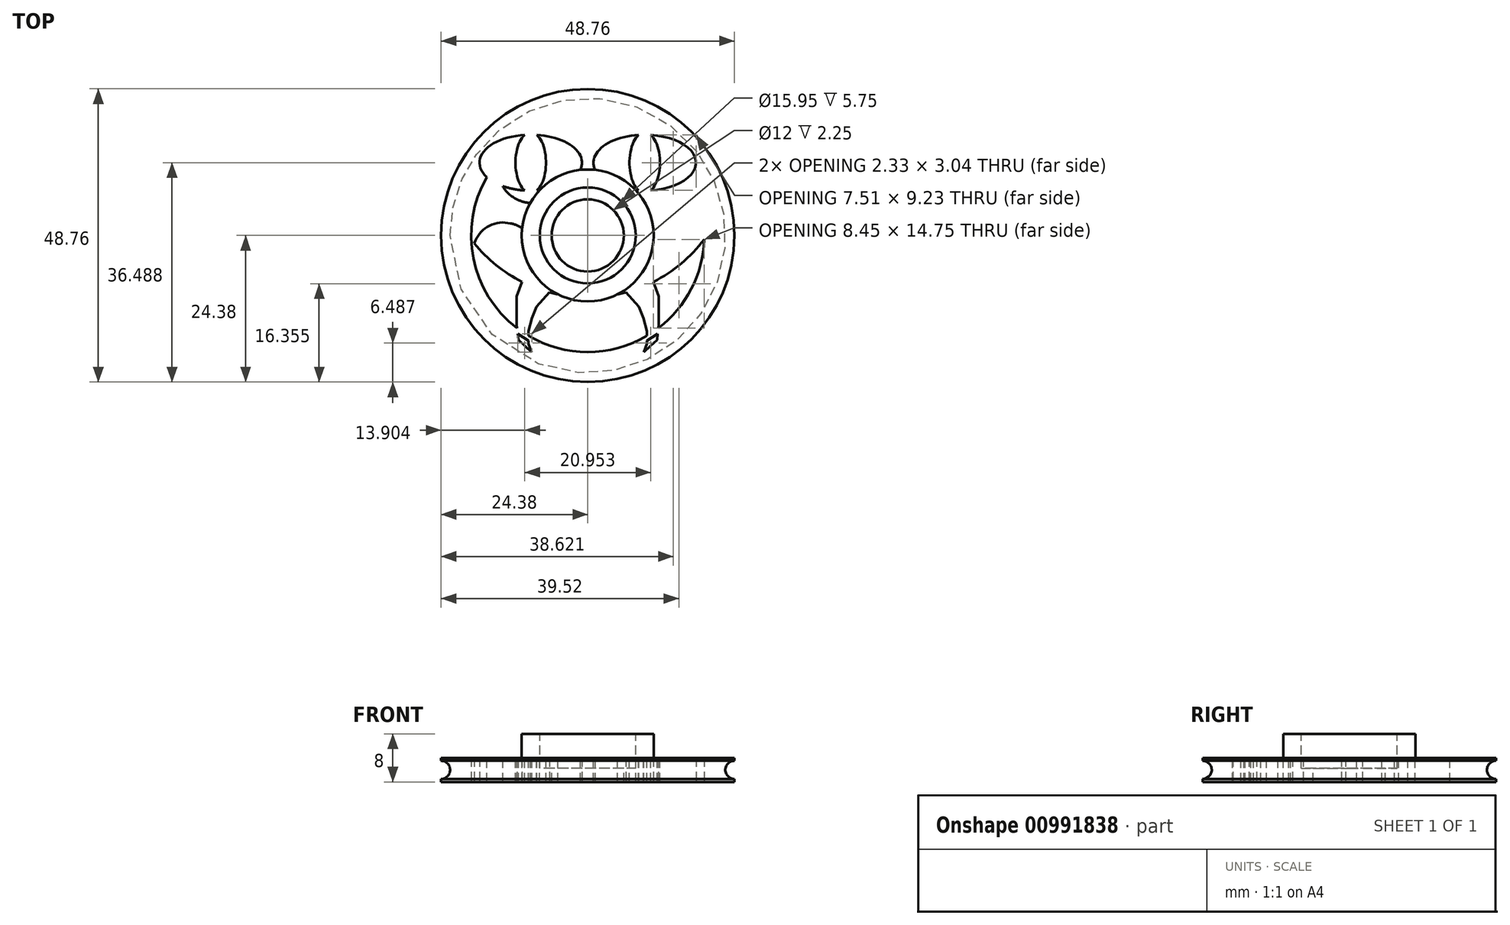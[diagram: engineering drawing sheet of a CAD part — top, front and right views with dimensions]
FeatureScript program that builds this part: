
annotation { "Feature Type Name" : "Feature", "Feature Type Description" : "" }
export const myFeature = defineFeature(function(context is Context, id is Id, definition is map)
    precondition{}
    {
        {
            var Q0;
            Q0=qCreatedBy(makeId("Top.planeOp"),FACE);
            var sketch = newSketch(context, id + "F0", { "sketchPlane" : qUnion([Q0])});
            skCircle(sketch, "E0", {"center": v(0, 0) * mm, "radius": 24.38 * mm});
            skCircle(sketch, "E1", {"center": v(0, 0) * mm, "radius": 8 * mm});
            skArc(sketch, "E2", {"start": v(-4.5, 7.8) * mm, "mid": v(0, -9) * mm, "end": v(4.5, 7.8) * mm});
            skArc(sketch, "E3.0", {"start": v(-9.52, 16.88) * mm, "mid": v(0, -19.38) * mm, "end": v(9.52, 16.88) * mm});
            skLineSegment(sketch, "E4.0", {"start": v(-2.12, 13.29) * mm, "end": v(-2.06, 12.89) * mm});
            skLineSegment(sketch, "E5.0", {"start": v(2.12, 13.29) * mm, "end": v(2.06, 12.89) * mm});
            skPoint(sketch, "E6.orphan", {"position": v(0, 21.65) * mm});
            skPoint(sketch, "E7.visualSharp", {"position": v(-1.44, 8.88) * mm});
            skArc(sketch, "E7.filletArc", {"start": v(-4.5, 7.8) * mm, "mid": v(-2.5, 9.96) * mm, "end": v(-2.06, 12.89) * mm});
            skPoint(sketch, "E8.visualSharp", {"position": v(1.44, 8.88) * mm});
            skArc(sketch, "E8.filletArc", {"start": v(2.06, 12.89) * mm, "mid": v(2.5, 9.96) * mm, "end": v(4.5, 7.8) * mm});
            skPoint(sketch, "E9.visualSharp", {"position": v(3.03, 19.14) * mm});
            skArc(sketch, "E9.filletArc", {"start": v(9.52, 16.88) * mm, "mid": v(4.88, 17.02) * mm, "end": v(2.12, 13.29) * mm});
            skPoint(sketch, "E10.visualSharp", {"position": v(-3.03, 19.14) * mm});
            skArc(sketch, "E10.filletArc", {"start": v(-2.12, 13.29) * mm, "mid": v(-4.88, 17.02) * mm, "end": v(-9.52, 16.88) * mm});
            skArc(sketch, "E11.1.0", {"start": v(-13.3, 2.09) * mm, "mid": v(-17.7, 0.62) * mm, "end": v(-19, -3.84) * mm});
            skLineSegment(sketch, "E11.1.1", {"start": v(-13.3, 2.09) * mm, "end": v(-12.9, 2.02) * mm});
            skArc(sketch, "E11.1.2", {"start": v(-8.8, -1.87) * mm, "mid": v(-10.25, 0.71) * mm, "end": v(-12.9, 2.02) * mm});
            skArc(sketch, "E11.1.3", {"start": v(-11.62, 5.94) * mm, "mid": v(-8.7, 5.45) * mm, "end": v(-6.02, 6.69) * mm});
            skLineSegment(sketch, "E11.1.4", {"start": v(-11.98, 6.12) * mm, "end": v(-11.62, 5.94) * mm});
            skArc(sketch, "E11.1.5", {"start": v(-13.1, 14.27) * mm, "mid": v(-14.68, 9.9) * mm, "end": v(-11.98, 6.12) * mm});
            skArc(sketch, "E11.2.0", {"start": v(-6.1, -12) * mm, "mid": v(-6.06, -16.64) * mm, "end": v(-2.22, -19.25) * mm});
            skLineSegment(sketch, "E11.2.1", {"start": v(-6.1, -12) * mm, "end": v(-5.91, -11.64) * mm});
            skArc(sketch, "E11.2.2", {"start": v(-0.94, -8.95) * mm, "mid": v(-3.84, -9.53) * mm, "end": v(-5.91, -11.64) * mm});
            skArc(sketch, "E11.2.3", {"start": v(-9.24, -9.22) * mm, "mid": v(-7.87, -6.6) * mm, "end": v(-8.22, -3.66) * mm});
            skLineSegment(sketch, "E11.2.4", {"start": v(-9.52, -9.5) * mm, "end": v(-9.24, -9.22) * mm});
            skArc(sketch, "E11.2.5", {"start": v(-17.62, -8.06) * mm, "mid": v(-13.95, -10.9) * mm, "end": v(-9.52, -9.5) * mm});
            skArc(sketch, "E11.3.0", {"start": v(9.52, -9.5) * mm, "mid": v(13.95, -10.9) * mm, "end": v(17.62, -8.06) * mm});
            skLineSegment(sketch, "E11.3.1", {"start": v(9.52, -9.5) * mm, "end": v(9.24, -9.22) * mm});
            skArc(sketch, "E11.3.2", {"start": v(8.22, -3.66) * mm, "mid": v(7.87, -6.6) * mm, "end": v(9.24, -9.22) * mm});
            skArc(sketch, "E11.3.3", {"start": v(5.91, -11.64) * mm, "mid": v(3.84, -9.53) * mm, "end": v(0.94, -8.95) * mm});
            skLineSegment(sketch, "E11.3.4", {"start": v(6.1, -12) * mm, "end": v(5.91, -11.64) * mm});
            skArc(sketch, "E11.3.5", {"start": v(2.22, -19.25) * mm, "mid": v(6.06, -16.64) * mm, "end": v(6.1, -12) * mm});
            skArc(sketch, "E11.4.0", {"start": v(11.98, 6.12) * mm, "mid": v(14.68, 9.9) * mm, "end": v(13.1, 14.27) * mm});
            skLineSegment(sketch, "E11.4.1", {"start": v(11.98, 6.12) * mm, "end": v(11.62, 5.94) * mm});
            skArc(sketch, "E11.4.2", {"start": v(6.02, 6.69) * mm, "mid": v(8.7, 5.45) * mm, "end": v(11.62, 5.94) * mm});
            skArc(sketch, "E11.4.3", {"start": v(12.9, 2.02) * mm, "mid": v(10.25, 0.71) * mm, "end": v(8.8, -1.87) * mm});
            skLineSegment(sketch, "E11.4.4", {"start": v(13.3, 2.09) * mm, "end": v(12.9, 2.02) * mm});
            skArc(sketch, "E11.4.5", {"start": v(19, -3.84) * mm, "mid": v(17.7, 0.62) * mm, "end": v(13.3, 2.09) * mm});
            skCircle(sketch, "E12", {"center": v(0, 13.95) * mm, "radius": 24.25 * mm});
            skSolve(sketch);
        }
        {
            var Q0;
            Q0=makeQuery(id+"F0.imprint","IMPRINT",FACE,{"disambiguationData":[TD([[makeQuery(id+"F0.imprint","IMPRINT",EDGE,{"derivedFrom":sQuery(id+"F0.wireOp",EDGE,"E0")}),1.0]])]});
            var Q1;
            {var subQ0=sQuery(id+"F0.wireOp",EDGE,"E11.4.0");Q1=makeQuery(id+"F0.imprint","IMPRINT",FACE,{"disambiguationData":[TD([[makeQuery(id+"F0.imprint","IMPRINT",EDGE,{"derivedFrom":subQ0}),-1.0]])]});}
            var Q2;
            Q2=makeQuery(id+"F0.imprint","IMPRINT",FACE,{"disambiguationData":[TD([[makeQuery(id+"F0.imprint","IMPRINT",EDGE,{"derivedFrom":sQuery(id+"F0.wireOp",EDGE,"E1")}),-1.0]])]});
            var Q3;
            {var subQ0=sQuery(id+"F0.wireOp",EDGE,"E11.1.1");Q3=makeQuery(id+"F0.imprint","IMPRINT",FACE,{"disambiguationData":[TD([[makeQuery(id+"F0.imprint","IMPRINT",EDGE,{"derivedFrom":subQ0}),1.0]])]});}
            var Q4;
            {var subQ1=sQuery(id+"F0.wireOp",EDGE,"E11.2.3");Q4=makeQuery(id+"F0.imprint","IMPRINT",FACE,{"disambiguationData":[TD([[makeQuery(id+"F0.imprint","IMPRINT",EDGE,{"derivedFrom":subQ1}),-1.0]])]});}
            var Q5;
            {var subQ5=sQuery(id+"F0.wireOp",EDGE,"E11.3.2");Q5=makeQuery(id+"F0.imprint","IMPRINT",FACE,{"disambiguationData":[TD([[makeQuery(id+"F0.imprint","IMPRINT",EDGE,{"derivedFrom":subQ5}),-1.0]])]});}
            var Q6;
            {var subQ1=sQuery(id+"F0.wireOp",EDGE,"E11.1.1");Q6=makeQuery(id+"F0.imprint","IMPRINT",FACE,{"disambiguationData":[TD([[makeQuery(id+"F0.imprint","IMPRINT",EDGE,{"derivedFrom":subQ1}),-1.0]])]});}
            var Q7;
            {var subQ0=sQuery(id+"F0.wireOp",EDGE,"E11.2.2");var subQ1=sQuery(id+"F0.wireOp",EDGE,"E2");var subQ2=makeQuery(id+"F0.imprint","INTERSECT",VERTEX,{"derivedFrom":[subQ1,subQ0]});Q7=makeQuery(id+"F0.imprint","IMPRINT",FACE,{"disambiguationData":[TD([[makeQuery(id+"F0.imprint","IMPRINT",EDGE,{"disambiguationData":[TD([[subQ2,-1.0]])],"derivedFrom":subQ1}),-1.0]])]});}
            var Q8;
            {var subQ0=sQuery(id+"F0.wireOp",EDGE,"E11.4.3");Q8=makeQuery(id+"F0.imprint","IMPRINT",FACE,{"disambiguationData":[TD([[makeQuery(id+"F0.imprint","IMPRINT",EDGE,{"derivedFrom":subQ0}),1.0]])]});}
            extrude(context, id + "F1", {"entities" : qUnion([Q0, Q1, Q2, Q3, Q4, Q5, Q6, Q7, Q8]), "depth" : 4 * mm, "offsetDistance" : 25.4 * mm, "symmetric" : true});
        }
        {
            var Q0;
            Q0=qCreatedBy(makeId("Top.planeOp"),FACE);
            var sketch = newSketch(context, id + "F2", { "sketchPlane" : qUnion([Q0])});
            skLineSegment(sketch, "E13", {"start": v(-14.44, -5.48) * mm, "end": v(-16.84, -9.61) * mm});
            skLineSegment(sketch, "E14", {"start": v(-16.84, -9.61) * mm, "end": v(-15.72, -11.69) * mm});
            skLineSegment(sketch, "E15", {"start": v(-15.72, -11.69) * mm, "end": v(-12.24, -6.68) * mm});
            skLineSegment(sketch, "E16", {"start": v(-12.24, -6.68) * mm, "end": v(-9.08, -8.27) * mm});
            skLineSegment(sketch, "E17", {"start": v(-9.08, -8.27) * mm, "end": v(-12.78, -12.6) * mm});
            skLineSegment(sketch, "E18", {"start": v(-12.78, -12.6) * mm, "end": v(-13.23, -11.08) * mm});
            skLineSegment(sketch, "E19", {"start": v(-13.23, -11.08) * mm, "end": v(-14.16, -11.08) * mm});
            skLineSegment(sketch, "E20", {"start": v(-14.16, -11.08) * mm, "end": v(-14.82, -11.08) * mm});
            skLineSegment(sketch, "E21", {"start": v(-14.82, -11.08) * mm, "end": v(-15.14, -10.86) * mm});
            skLineSegment(sketch, "E22", {"start": v(-4.98, -9.03) * mm, "end": v(-8.45, -15.68) * mm});
            skLineSegment(sketch, "E23", {"start": v(-1.8, -17.1) * mm, "end": v(-0.72, -9.57) * mm});
            skLineSegment(sketch, "E24", {"start": v(0.8, -9.78) * mm, "end": v(1.77, -17.83) * mm});
            skLineSegment(sketch, "E25", {"start": v(6.47, -15.97) * mm, "end": v(4.75, -8.64) * mm});
            skLineSegment(sketch, "E26", {"start": v(-8.6, -8.27) * mm, "end": v(-13.47, -13.99) * mm});
            skLineSegment(sketch, "E27", {"start": v(-13.47, -13.99) * mm, "end": v(-12.24, -13.99) * mm});
            skLineSegment(sketch, "E28", {"start": v(-12.24, -13.99) * mm, "end": v(-11.5, -14.36) * mm});
            skLineSegment(sketch, "E29", {"start": v(-11.5, -14.36) * mm, "end": v(-11.43, -15.48) * mm});
            skLineSegment(sketch, "E30", {"start": v(-11.43, -15.48) * mm, "end": v(-11, -16.02) * mm});
            skLineSegment(sketch, "E31", {"start": v(-11, -16.02) * mm, "end": v(-10.2, -16.27) * mm});
            skLineSegment(sketch, "E32", {"start": v(-10.2, -16.27) * mm, "end": v(-7.92, -13.58) * mm});
            skLineSegment(sketch, "E33", {"start": v(-7.92, -13.58) * mm, "end": v(-6.92, -11.6) * mm});
            skLineSegment(sketch, "E34", {"start": v(-6.92, -11.6) * mm, "end": v(-6.1, -8.93) * mm});
            skLineSegment(sketch, "E35", {"start": v(5.83, -9.57) * mm, "end": v(6.89, -14.1) * mm});
            skLineSegment(sketch, "E36", {"start": v(6.89, -14.1) * mm, "end": v(11.16, -12.01) * mm});
            skLineSegment(sketch, "E37", {"start": v(11.16, -12.01) * mm, "end": v(10.22, -7.97) * mm});
            skLineSegment(sketch, "E38", {"start": v(10.22, -7.97) * mm, "end": v(13.16, -14.55) * mm});
            skLineSegment(sketch, "E39", {"start": v(13.16, -14.55) * mm, "end": v(14.29, -13.09) * mm});
            skLineSegment(sketch, "E40", {"start": v(14.29, -13.09) * mm, "end": v(15.36, -10.64) * mm});
            skLineSegment(sketch, "E41", {"start": v(15.36, -10.64) * mm, "end": v(14.11, -10.46) * mm});
            skLineSegment(sketch, "E42", {"start": v(14.11, -10.46) * mm, "end": v(13.16, -9.57) * mm});
            skLineSegment(sketch, "E43", {"start": v(13.16, -9.57) * mm, "end": v(13.16, -7.95) * mm});
            skLineSegment(sketch, "E44", {"start": v(13.16, -7.95) * mm, "end": v(13.02, -6.39) * mm});
            skLineSegment(sketch, "E45", {"start": v(-14.44, -5.48) * mm, "end": v(-12.24, -6.68) * mm});
            skLineSegment(sketch, "E46", {"start": v(-8.6, -8.27) * mm, "end": v(-6.1, -8.93) * mm});
            skLineSegment(sketch, "E47", {"start": v(-4.98, -9.03) * mm, "end": v(-0.72, -9.57) * mm});
            skLineSegment(sketch, "E48", {"start": v(0.8, -9.78) * mm, "end": v(4.75, -8.64) * mm});
            skLineSegment(sketch, "E49", {"start": v(5.83, -9.57) * mm, "end": v(10.22, -7.97) * mm});
            skLineSegment(sketch, "E50", {"start": v(10.22, -7.97) * mm, "end": v(13.02, -6.39) * mm});
            skLineSegment(sketch, "E51", {"start": v(13.52, -5.97) * mm, "end": v(14.5, -8.94) * mm});
            skLineSegment(sketch, "E52", {"start": v(14.5, -8.94) * mm, "end": v(15.67, -8.94) * mm});
            skLineSegment(sketch, "E53", {"start": v(15.67, -8.94) * mm, "end": v(16.95, -8.28) * mm});
            skLineSegment(sketch, "E54", {"start": v(16.95, -8.28) * mm, "end": v(17.81, -7.9) * mm});
            skLineSegment(sketch, "E55", {"start": v(17.81, -7.9) * mm, "end": v(18.02, -7.07) * mm});
            skLineSegment(sketch, "E56", {"start": v(18.02, -7.07) * mm, "end": v(17.67, -6.3) * mm});
            skLineSegment(sketch, "E57", {"start": v(17.67, -6.3) * mm, "end": v(17.06, -4.94) * mm});
            skLineSegment(sketch, "E58", {"start": v(17.06, -4.94) * mm, "end": v(16.19, -3.72) * mm});
            skLineSegment(sketch, "E59", {"start": v(16.19, -3.72) * mm, "end": v(13.52, -5.97) * mm});
            skLineSegment(sketch, "E60", {"start": v(-8.45, -15.68) * mm, "end": v(-6.08, -16.91) * mm});
            skLineSegment(sketch, "E61", {"start": v(-6.08, -16.91) * mm, "end": v(-4.84, -18.74) * mm});
            skLineSegment(sketch, "E62", {"start": v(-4.84, -18.74) * mm, "end": v(-3.33, -19.9) * mm});
            skLineSegment(sketch, "E63", {"start": v(-3.33, -19.9) * mm, "end": v(-1.8, -17.1) * mm});
            skLineSegment(sketch, "E64", {"start": v(11.16, -12.01) * mm, "end": v(11.88, -11.69) * mm});
            skLineSegment(sketch, "E65", {"start": v(1.77, -17.83) * mm, "end": v(3.1, -17.67) * mm});
            skLineSegment(sketch, "E66", {"start": v(3.1, -17.67) * mm, "end": v(3.94, -18.9) * mm});
            skLineSegment(sketch, "E67", {"start": v(3.94, -18.9) * mm, "end": v(5.39, -18.9) * mm});
            skLineSegment(sketch, "E68", {"start": v(5.39, -18.9) * mm, "end": v(5.39, -17.83) * mm});
            skLineSegment(sketch, "E69", {"start": v(5.84, -13.31) * mm, "end": v(6.47, -15.97) * mm});
            skLineSegment(sketch, "E70", {"start": v(5.39, -17.83) * mm, "end": v(6.5, -17.3) * mm});
            skLineSegment(sketch, "E71", {"start": v(6.5, -17.3) * mm, "end": v(6.47, -15.97) * mm});
            skSolve(sketch);
        }
        {
            var Q0;
            Q0=qCreatedBy(makeId("Top.planeOp"),FACE);
            var sketch = newSketch(context, id + "F3", { "sketchPlane" : qUnion([Q0])});
            skEllipse(sketch, "E72", {"center": v(-9.48, 12.1) * mm, "majorRadius": 8.52 * mm, "minorRadius": 4.65 * mm, "majorAxis": v(-1, 0)});
            skEllipse(sketch, "E73.MirrorC", {"center": v(9.48, 12.1) * mm, "majorRadius": 8.52 * mm, "minorRadius": 4.65 * mm, "majorAxis": v(1, 0)});
            skSolve(sketch);
        }
        {
            var Q0;
            Q0=makeQuery(id+"F0.imprint","IMPRINT",FACE,{"disambiguationData":[TD([[makeQuery(id+"F0.imprint","IMPRINT",EDGE,{"derivedFrom":sQuery(id+"F0.wireOp",EDGE,"E1")}),-1.0]])]});
            var Q1;
            {var subQ0=sQuery(id+"F0.wireOp",EDGE,"E11.1.1");Q1=makeQuery(id+"F0.imprint","IMPRINT",FACE,{"disambiguationData":[TD([[makeQuery(id+"F0.imprint","IMPRINT",EDGE,{"derivedFrom":subQ0}),1.0]])]});}
            var Q2;
            {var subQ0=sQuery(id+"F0.wireOp",EDGE,"E11.4.0");Q2=makeQuery(id+"F0.imprint","IMPRINT",FACE,{"disambiguationData":[TD([[makeQuery(id+"F0.imprint","IMPRINT",EDGE,{"derivedFrom":subQ0}),-1.0]])]});}
            var Q3;
            Q3=makeQuery(id+"F0.imprint","IMPRINT",FACE,{"disambiguationData":[TD([[makeQuery(id+"F0.imprint","IMPRINT",EDGE,{"derivedFrom":sQuery(id+"F0.wireOp",EDGE,"E5.0")}),1.0]])]});
            var Q4;
            Q4=makeQuery(id+"F0.imprint","IMPRINT",FACE,{"disambiguationData":[TD([[makeQuery(id+"F0.imprint","IMPRINT",EDGE,{"derivedFrom":sQuery(id+"F0.wireOp",EDGE,"E4.0")}),-1.0]])]});
            extrude(context, id + "F4", {"entities" : qUnion([Q0, Q1, Q2, Q3, Q4]), "operationType" : NewBodyOperationType.ADD, "depth" : 4 * mm, "offsetDistance" : 25.4 * mm, "symmetric" : true});
        }
        {
            var Q0;
            Q0=qSketchRegion(id+"F3",true);
            extrude(context, id + "F5", {"entities" : qUnion([Q0]), "operationType" : NewBodyOperationType.REMOVE, "oppositeDirection" : true, "depth" : 5 * mm, "offsetDistance" : 25.4 * mm, "symmetric" : true});
        }
        {
            var Q0;
            {var subQ0=sQuery(id+"F0.wireOp",EDGE,"E12");var subQ1=sQuery(id+"F0.wireOp",EDGE,"E11.1.0");var subQ2=sQuery(id+"F0.wireOp",EDGE,"E2");var subQ3=sQuery(id+"F0.wireOp",EDGE,"E1");var subQ4=sQuery(id+"F0.wireOp",EDGE,"E0");Q0=makeQuery(id+"F4.boolean.opBoolean","MERGE",FACE,{"derivedFrom":[makeQuery(id+"F1.opExtrude","CAP_FACE",FACE,{"disambiguationData":[OSD([subQ4,subQ3,subQ2,sQuery(id+"F0.wireOp",EDGE,"E3.0"),sQuery(id+"F0.wireOp",EDGE,"E4.0"),sQuery(id+"F0.wireOp",EDGE,"E5.0"),sQuery(id+"F0.wireOp",EDGE,"E7.filletArc"),sQuery(id+"F0.wireOp",EDGE,"E8.filletArc"),sQuery(id+"F0.wireOp",EDGE,"E9.filletArc"),sQuery(id+"F0.wireOp",EDGE,"E10.filletArc"),subQ1,sQuery(id+"F0.wireOp",EDGE,"E11.1.3"),sQuery(id+"F0.wireOp",EDGE,"E11.1.4"),sQuery(id+"F0.wireOp",EDGE,"E11.1.5"),sQuery(id+"F0.wireOp",EDGE,"E11.4.0"),sQuery(id+"F0.wireOp",EDGE,"E11.4.1"),sQuery(id+"F0.wireOp",EDGE,"E11.4.2"),subQ0])],"isStart":false}),makeQuery(id+"F4.opExtrude","CAP_FACE",FACE,{"disambiguationData":[OSD([subQ4,subQ3,subQ2,subQ1,sQuery(id+"F0.wireOp",EDGE,"E11.1.1"),sQuery(id+"F0.wireOp",EDGE,"E11.1.2"),sQuery(id+"F0.wireOp",EDGE,"E11.4.3"),sQuery(id+"F0.wireOp",EDGE,"E11.4.4"),sQuery(id+"F0.wireOp",EDGE,"E11.4.5"),subQ0])],"isStart":false})]});}
            var sketch = newSketch(context, id + "F6", { "sketchPlane" : qUnion([Q0])});
            skLineSegment(sketch, "E74", {"start": v(-10.73, -7.2) * mm, "end": v(-11.83, -10.11) * mm});
            skLineSegment(sketch, "E75", {"start": v(-11.83, -10.11) * mm, "end": v(-11.83, -13.22) * mm});
            skLineSegment(sketch, "E76", {"start": v(-11.83, -13.22) * mm, "end": v(-11.83, -14.74) * mm});
            skLineSegment(sketch, "E77", {"start": v(-11.83, -14.74) * mm, "end": v(-11.21, -16.75) * mm});
            skLineSegment(sketch, "E78", {"start": v(-11.21, -16.75) * mm, "end": v(-9.83, -18) * mm});
            skLineSegment(sketch, "E79", {"start": v(-9.83, -18) * mm, "end": v(-9.83, -15.92) * mm});
            skLineSegment(sketch, "E80", {"start": v(-9.83, -15.92) * mm, "end": v(-9.28, -13.78) * mm});
            skLineSegment(sketch, "E81", {"start": v(-9.28, -13.78) * mm, "end": v(-8.51, -11.84) * mm});
            skLineSegment(sketch, "E82", {"start": v(-8.51, -11.84) * mm, "end": v(-7.06, -10.22) * mm});
            skLineSegment(sketch, "E83", {"start": v(-7.06, -10.22) * mm, "end": v(-6.26, -9.33) * mm});
            skLineSegment(sketch, "E84", {"start": v(-6.26, -9.33) * mm, "end": v(-5.61, -7.98) * mm});
            skLineSegment(sketch, "E85", {"start": v(-5.61, -7.98) * mm, "end": v(-9.83, -5.47) * mm});
            skLineSegment(sketch, "E86", {"start": v(-9.83, -5.47) * mm, "end": v(-10.73, -7.2) * mm});
            skLineSegment(sketch, "E87", {"start": v(-11.83, -14.74) * mm, "end": v(-11.52, -17.36) * mm});
            skPoint(sketch, "E87.endSnap0", {"position": v(-11.52, -15.75) * mm});
            skLineSegment(sketch, "E88", {"start": v(-11.52, -17.36) * mm, "end": v(-10.42, -18.39) * mm});
            skLineSegment(sketch, "E89", {"start": v(-10.42, -18.39) * mm, "end": v(-9.31, -19.41) * mm});
            skLineSegment(sketch, "E90", {"start": v(-9.31, -19.41) * mm, "end": v(-9.83, -18) * mm});
            skLineSegment(sketch, "E91", {"start": v(-9.83, -17.52) * mm, "end": v(-11.6, -16.66) * mm});
            skLineSegment(sketch, "E92", {"start": v(-9.83, -16.96) * mm, "end": v(-11.71, -15.78) * mm});
            skLineSegment(sketch, "E93.MirrorCS", {"start": v(5.61, -7.98) * mm, "end": v(9.83, -5.47) * mm});
            skLineSegment(sketch, "E94.MirrorCS", {"start": v(9.83, -5.47) * mm, "end": v(10.73, -7.2) * mm});
            skLineSegment(sketch, "E95.MirrorCS", {"start": v(10.73, -7.2) * mm, "end": v(11.83, -10.11) * mm});
            skLineSegment(sketch, "E96.MirrorCS", {"start": v(11.83, -10.11) * mm, "end": v(11.83, -13.22) * mm});
            skLineSegment(sketch, "E97.MirrorCS", {"start": v(11.83, -13.22) * mm, "end": v(11.83, -14.74) * mm});
            skLineSegment(sketch, "E98.MirrorCS", {"start": v(11.83, -14.74) * mm, "end": v(11.52, -17.36) * mm});
            skLineSegment(sketch, "E99.MirrorCS", {"start": v(11.52, -17.36) * mm, "end": v(10.42, -18.39) * mm});
            skLineSegment(sketch, "E100.MirrorCS", {"start": v(10.42, -18.39) * mm, "end": v(9.31, -19.41) * mm});
            skLineSegment(sketch, "E101.MirrorCS", {"start": v(9.31, -19.41) * mm, "end": v(9.83, -18) * mm});
            skLineSegment(sketch, "E102.MirrorCS", {"start": v(9.83, -15.92) * mm, "end": v(9.28, -13.78) * mm});
            skLineSegment(sketch, "E103.MirrorCS", {"start": v(9.28, -13.78) * mm, "end": v(8.51, -11.84) * mm});
            skLineSegment(sketch, "E104.MirrorCS", {"start": v(8.51, -11.84) * mm, "end": v(7.06, -10.22) * mm});
            skLineSegment(sketch, "E105.MirrorCS", {"start": v(7.06, -10.22) * mm, "end": v(6.26, -9.33) * mm});
            skLineSegment(sketch, "E106.MirrorCS", {"start": v(6.26, -9.33) * mm, "end": v(5.61, -7.98) * mm});
            skLineSegment(sketch, "E107.MirrorCS", {"start": v(9.83, -18) * mm, "end": v(9.83, -15.92) * mm});
            skLineSegment(sketch, "E108.MirrorCS", {"start": v(9.83, -16.96) * mm, "end": v(11.71, -15.78) * mm});
            skLineSegment(sketch, "E109.MirrorCS", {"start": v(11.21, -16.75) * mm, "end": v(9.83, -18) * mm});
            skLineSegment(sketch, "E110.MirrorCS", {"start": v(9.83, -17.52) * mm, "end": v(11.6, -16.66) * mm});
            skSolve(sketch);
        }
        {
            var Q0;
            Q0=qSketchRegion(id+"F6",true);
            extrude(context, id + "F7", {"entities" : qUnion([Q0]), "operationType" : NewBodyOperationType.ADD, "oppositeDirection" : true, "depth" : 4 * mm, "offsetDistance" : 25.4 * mm});
        }
        {
            var Q0;
            {var subQ3=sQuery(id+"F6.wireOp",EDGE,"E78");var subQ5=sQuery(id+"F6.wireOp",EDGE,"E77");var subQ6=makeQuery(id+"F6.imprint","INTERSECT",VERTEX,{"derivedFrom":[subQ5,subQ3]});Q0=makeQuery(id+"F6.imprint","IMPRINT",FACE,{"disambiguationData":[TD([[makeQuery(id+"F6.imprint","IMPRINT",EDGE,{"disambiguationData":[TD([[subQ6,1.0]])],"derivedFrom":subQ5}),-1.0]])]});}
            var Q1;
            {var subQ3=sQuery(id+"F6.wireOp",EDGE,"E78");var subQ5=sQuery(id+"F6.wireOp",EDGE,"E77");var subQ6=makeQuery(id+"F6.imprint","INTERSECT",VERTEX,{"derivedFrom":[subQ5,subQ3]});Q1=makeQuery(id+"F6.imprint","IMPRINT",FACE,{"disambiguationData":[TD([[makeQuery(id+"F6.imprint","IMPRINT",EDGE,{"disambiguationData":[TD([[subQ6,1.0]])],"derivedFrom":subQ5}),1.0]])]});}
            var Q2;
            {var subQ0=sQuery(id+"F6.wireOp",EDGE,"E79");var subQ3=sQuery(id+"F6.wireOp",EDGE,"E91");var subQ5=makeQuery(id+"F6.imprint","INTERSECT",VERTEX,{"derivedFrom":[subQ0,subQ3]});Q2=makeQuery(id+"F6.imprint","IMPRINT",FACE,{"disambiguationData":[TD([[makeQuery(id+"F6.imprint","IMPRINT",EDGE,{"disambiguationData":[TD([[subQ5,-1.0]])],"derivedFrom":subQ3}),1.0]])]});}
            var Q3;
            {var subQ0=sQuery(id+"F6.wireOp",EDGE,"E88");Q3=makeQuery(id+"F6.imprint","IMPRINT",FACE,{"disambiguationData":[TD([[makeQuery(id+"F6.imprint","IMPRINT",EDGE,{"derivedFrom":subQ0}),1.0]])]});}
            var Q4;
            {var subQ1=sQuery(id+"F6.wireOp",EDGE,"E107.MirrorCS");var subQ3=sQuery(id+"F6.wireOp",EDGE,"E110.MirrorCS");var subQ4=makeQuery(id+"F6.imprint","INTERSECT",VERTEX,{"derivedFrom":[subQ1,subQ3]});Q4=makeQuery(id+"F6.imprint","IMPRINT",FACE,{"disambiguationData":[TD([[makeQuery(id+"F6.imprint","IMPRINT",EDGE,{"disambiguationData":[TD([[subQ4,-1.0]])],"derivedFrom":subQ3}),-1.0]])]});}
            var Q5;
            {var subQ1=sQuery(id+"F6.wireOp",EDGE,"E99.MirrorCS");Q5=makeQuery(id+"F6.imprint","IMPRINT",FACE,{"disambiguationData":[TD([[makeQuery(id+"F6.imprint","IMPRINT",EDGE,{"derivedFrom":subQ1}),-1.0]])]});}
            var Q6;
            {var subQ4=sQuery(id+"F6.wireOp",EDGE,"E108.MirrorCS");Q6=makeQuery(id+"F6.imprint","IMPRINT",FACE,{"disambiguationData":[TD([[makeQuery(id+"F6.imprint","IMPRINT",EDGE,{"derivedFrom":subQ4}),-1.0]])]});}
            extrude(context, id + "F8", {"entities" : qUnion([Q0, Q1, Q2, Q3, Q4, Q5, Q6]), "operationType" : NewBodyOperationType.REMOVE, "oppositeDirection" : true, "depth" : 25.4 * mm, "offsetDistance" : 25.4 * mm});
        }
        {
            var Q0;
            Q0=qCreatedBy(makeId("Front.planeOp"),FACE);
            var sketch = newSketch(context, id + "F9", { "sketchPlane" : qUnion([Q0])});
            skCircle(sketch, "E111", {"center": v(-24.38, 0) * mm, "radius": 1.5 * mm});
            skLineSegment(sketch, "E112", {"start": v(0, 3.3) * mm, "end": v(0, -4.33) * mm, "construction": true});
            skSolve(sketch);
        }
        {
            var Q0;
            {var subQ0=sQuery(id+"F0.wireOp",EDGE,"E12");var subQ1=sQuery(id+"F0.wireOp",EDGE,"E11.1.0");var subQ2=sQuery(id+"F0.wireOp",EDGE,"E2");var subQ3=sQuery(id+"F0.wireOp",EDGE,"E1");var subQ4=sQuery(id+"F0.wireOp",EDGE,"E0");Q0=makeQuery(id+"F7.boolean.opBoolean","MERGE",FACE,{"derivedFrom":[makeQuery(id+"F4.boolean.opBoolean","MERGE",FACE,{"derivedFrom":[makeQuery(id+"F1.opExtrude","CAP_FACE",FACE,{"disambiguationData":[OSD([subQ4,subQ3,subQ2,sQuery(id+"F0.wireOp",EDGE,"E3.0"),sQuery(id+"F0.wireOp",EDGE,"E4.0"),sQuery(id+"F0.wireOp",EDGE,"E5.0"),sQuery(id+"F0.wireOp",EDGE,"E7.filletArc"),sQuery(id+"F0.wireOp",EDGE,"E8.filletArc"),sQuery(id+"F0.wireOp",EDGE,"E9.filletArc"),sQuery(id+"F0.wireOp",EDGE,"E10.filletArc"),subQ1,sQuery(id+"F0.wireOp",EDGE,"E11.1.3"),sQuery(id+"F0.wireOp",EDGE,"E11.1.4"),sQuery(id+"F0.wireOp",EDGE,"E11.1.5"),sQuery(id+"F0.wireOp",EDGE,"E11.4.0"),sQuery(id+"F0.wireOp",EDGE,"E11.4.1"),sQuery(id+"F0.wireOp",EDGE,"E11.4.2"),subQ0])],"isStart":false}),makeQuery(id+"F4.opExtrude","CAP_FACE",FACE,{"disambiguationData":[OSD([subQ4,subQ3,subQ2,subQ1,sQuery(id+"F0.wireOp",EDGE,"E11.1.1"),sQuery(id+"F0.wireOp",EDGE,"E11.1.2"),sQuery(id+"F0.wireOp",EDGE,"E11.4.3"),sQuery(id+"F0.wireOp",EDGE,"E11.4.4"),sQuery(id+"F0.wireOp",EDGE,"E11.4.5"),subQ0])],"isStart":false})]}),makeQuery(id+"F7.opExtrude","CAP_FACE",FACE,{"disambiguationData":[OSD([sQuery(id+"F6.wireOp",EDGE,"E74"),sQuery(id+"F6.wireOp",EDGE,"E75"),sQuery(id+"F6.wireOp",EDGE,"E76"),sQuery(id+"F6.wireOp",EDGE,"E79"),sQuery(id+"F6.wireOp",EDGE,"E80"),sQuery(id+"F6.wireOp",EDGE,"E81"),sQuery(id+"F6.wireOp",EDGE,"E82"),sQuery(id+"F6.wireOp",EDGE,"E83"),sQuery(id+"F6.wireOp",EDGE,"E84"),sQuery(id+"F6.wireOp",EDGE,"E85"),sQuery(id+"F6.wireOp",EDGE,"E86"),sQuery(id+"F6.wireOp",EDGE,"E87"),sQuery(id+"F6.wireOp",EDGE,"E88"),sQuery(id+"F6.wireOp",EDGE,"E89"),sQuery(id+"F6.wireOp",EDGE,"E90")])],"isStart":true}),makeQuery(id+"F7.opExtrude","CAP_FACE",FACE,{"disambiguationData":[OSD([sQuery(id+"F6.wireOp",EDGE,"E93.MirrorCS"),sQuery(id+"F6.wireOp",EDGE,"E94.MirrorCS"),sQuery(id+"F6.wireOp",EDGE,"E95.MirrorCS"),sQuery(id+"F6.wireOp",EDGE,"E96.MirrorCS"),sQuery(id+"F6.wireOp",EDGE,"E97.MirrorCS"),sQuery(id+"F6.wireOp",EDGE,"E98.MirrorCS"),sQuery(id+"F6.wireOp",EDGE,"E99.MirrorCS"),sQuery(id+"F6.wireOp",EDGE,"E100.MirrorCS"),sQuery(id+"F6.wireOp",EDGE,"E101.MirrorCS"),sQuery(id+"F6.wireOp",EDGE,"E102.MirrorCS"),sQuery(id+"F6.wireOp",EDGE,"E103.MirrorCS"),sQuery(id+"F6.wireOp",EDGE,"E104.MirrorCS"),sQuery(id+"F6.wireOp",EDGE,"E105.MirrorCS"),sQuery(id+"F6.wireOp",EDGE,"E106.MirrorCS"),sQuery(id+"F6.wireOp",EDGE,"E107.MirrorCS")])],"isStart":true})]});}
            var sketch = newSketch(context, id + "F10", { "sketchPlane" : qUnion([Q0])});
            skEllipse(sketch, "E113", {"center": v(-9.48, 12.1) * mm, "majorRadius": 5.03 * mm, "minorRadius": 2.53 * mm, "majorAxis": v(0, -1)});
            skEllipse(sketch, "E114.MirrorC", {"center": v(9.48, 12.1) * mm, "majorRadius": 5.03 * mm, "minorRadius": 2.53 * mm, "majorAxis": v(0, -1)});
            skSolve(sketch);
        }
        {
            var Q0;
            Q0=qSketchRegion(id+"F10",true);
            extrude(context, id + "F11", {"entities" : qUnion([Q0]), "operationType" : NewBodyOperationType.ADD, "oppositeDirection" : true, "depth" : 4 * mm, "offsetDistance" : 25.4 * mm});
        }
        {
            var Q0;
            {var subQ0=sQuery(id+"F0.wireOp",EDGE,"E12");var subQ1=sQuery(id+"F0.wireOp",EDGE,"E11.1.0");var subQ2=sQuery(id+"F0.wireOp",EDGE,"E2");var subQ3=sQuery(id+"F0.wireOp",EDGE,"E1");var subQ4=sQuery(id+"F0.wireOp",EDGE,"E0");Q0=makeQuery(id+"F11.boolean.opBoolean","MERGE",FACE,{"derivedFrom":[makeQuery(id+"F7.boolean.opBoolean","MERGE",FACE,{"derivedFrom":[makeQuery(id+"F4.boolean.opBoolean","MERGE",FACE,{"derivedFrom":[makeQuery(id+"F1.opExtrude","CAP_FACE",FACE,{"disambiguationData":[OSD([subQ4,subQ3,subQ2,sQuery(id+"F0.wireOp",EDGE,"E3.0"),sQuery(id+"F0.wireOp",EDGE,"E4.0"),sQuery(id+"F0.wireOp",EDGE,"E5.0"),sQuery(id+"F0.wireOp",EDGE,"E7.filletArc"),sQuery(id+"F0.wireOp",EDGE,"E8.filletArc"),sQuery(id+"F0.wireOp",EDGE,"E9.filletArc"),sQuery(id+"F0.wireOp",EDGE,"E10.filletArc"),subQ1,sQuery(id+"F0.wireOp",EDGE,"E11.1.3"),sQuery(id+"F0.wireOp",EDGE,"E11.1.4"),sQuery(id+"F0.wireOp",EDGE,"E11.1.5"),sQuery(id+"F0.wireOp",EDGE,"E11.4.0"),sQuery(id+"F0.wireOp",EDGE,"E11.4.1"),sQuery(id+"F0.wireOp",EDGE,"E11.4.2"),subQ0])],"isStart":false}),makeQuery(id+"F4.opExtrude","CAP_FACE",FACE,{"disambiguationData":[OSD([subQ4,subQ3,subQ2,subQ1,sQuery(id+"F0.wireOp",EDGE,"E11.1.1"),sQuery(id+"F0.wireOp",EDGE,"E11.1.2"),sQuery(id+"F0.wireOp",EDGE,"E11.4.3"),sQuery(id+"F0.wireOp",EDGE,"E11.4.4"),sQuery(id+"F0.wireOp",EDGE,"E11.4.5"),subQ0])],"isStart":false})]}),makeQuery(id+"F7.opExtrude","CAP_FACE",FACE,{"disambiguationData":[OSD([sQuery(id+"F6.wireOp",EDGE,"E74"),sQuery(id+"F6.wireOp",EDGE,"E75"),sQuery(id+"F6.wireOp",EDGE,"E76"),sQuery(id+"F6.wireOp",EDGE,"E79"),sQuery(id+"F6.wireOp",EDGE,"E80"),sQuery(id+"F6.wireOp",EDGE,"E81"),sQuery(id+"F6.wireOp",EDGE,"E82"),sQuery(id+"F6.wireOp",EDGE,"E83"),sQuery(id+"F6.wireOp",EDGE,"E84"),sQuery(id+"F6.wireOp",EDGE,"E85"),sQuery(id+"F6.wireOp",EDGE,"E86"),sQuery(id+"F6.wireOp",EDGE,"E87"),sQuery(id+"F6.wireOp",EDGE,"E88"),sQuery(id+"F6.wireOp",EDGE,"E89"),sQuery(id+"F6.wireOp",EDGE,"E90")])],"isStart":true}),makeQuery(id+"F7.opExtrude","CAP_FACE",FACE,{"disambiguationData":[OSD([sQuery(id+"F6.wireOp",EDGE,"E93.MirrorCS"),sQuery(id+"F6.wireOp",EDGE,"E94.MirrorCS"),sQuery(id+"F6.wireOp",EDGE,"E95.MirrorCS"),sQuery(id+"F6.wireOp",EDGE,"E96.MirrorCS"),sQuery(id+"F6.wireOp",EDGE,"E97.MirrorCS"),sQuery(id+"F6.wireOp",EDGE,"E98.MirrorCS"),sQuery(id+"F6.wireOp",EDGE,"E99.MirrorCS"),sQuery(id+"F6.wireOp",EDGE,"E100.MirrorCS"),sQuery(id+"F6.wireOp",EDGE,"E101.MirrorCS"),sQuery(id+"F6.wireOp",EDGE,"E102.MirrorCS"),sQuery(id+"F6.wireOp",EDGE,"E103.MirrorCS"),sQuery(id+"F6.wireOp",EDGE,"E104.MirrorCS"),sQuery(id+"F6.wireOp",EDGE,"E105.MirrorCS"),sQuery(id+"F6.wireOp",EDGE,"E106.MirrorCS"),sQuery(id+"F6.wireOp",EDGE,"E107.MirrorCS")])],"isStart":true})]}),makeQuery(id+"F11.opExtrude","CAP_FACE",FACE,{"disambiguationData":[OSD([sQuery(id+"F10.wireOp",EDGE,"E113")])],"isStart":true}),makeQuery(id+"F11.opExtrude","CAP_FACE",FACE,{"disambiguationData":[OSD([sQuery(id+"F10.wireOp",EDGE,"E114.MirrorC")])],"isStart":true})]});}
            var sketch = newSketch(context, id + "F12", { "sketchPlane" : qUnion([Q0])});
            skLineSegment(sketch, "E115", {"start": v(-12.14, -16.06) * mm, "end": v(-9.04, -18) * mm});
            skLineSegment(sketch, "E116", {"start": v(-9.04, -18) * mm, "end": v(-9.83, -16.7) * mm});
            skLineSegment(sketch, "E117", {"start": v(-9.83, -16.7) * mm, "end": v(-11.71, -15.78) * mm});
            skLineSegment(sketch, "E118", {"start": v(-11.71, -15.78) * mm, "end": v(-12.14, -16.06) * mm});
            skLineSegment(sketch, "E119.MirrorCS", {"start": v(12.14, -16.06) * mm, "end": v(9.04, -18) * mm});
            skLineSegment(sketch, "E120.MirrorCS", {"start": v(9.04, -18) * mm, "end": v(9.83, -16.7) * mm});
            skLineSegment(sketch, "E121.MirrorCS", {"start": v(9.83, -16.7) * mm, "end": v(11.71, -15.78) * mm});
            skLineSegment(sketch, "E122.MirrorCS", {"start": v(11.71, -15.78) * mm, "end": v(12.14, -16.06) * mm});
            skSolve(sketch);
        }
        {
            var Q0;
            Q0=qSketchRegion(id+"F12",true);
            var Q1;
            {var subQ72=sQuery(id+"F12.wireOp",EDGE,"E116");Q1=makeQuery(id+"F12.imprint","IMPRINT",FACE,{"disambiguationData":[TD([[makeQuery(id+"F12.imprint","IMPRINT",EDGE,{"derivedFrom":subQ72}),-1.0]])]});}
            extrude(context, id + "F13", {"entities" : qUnion([Q0, Q1]), "operationType" : NewBodyOperationType.ADD, "oppositeDirection" : true, "depth" : 4 * mm, "offsetDistance" : 25.4 * mm});
        }
        {
            var Q0;
            {var subQ0=sQuery(id+"F0.wireOp",EDGE,"E12");var subQ1=sQuery(id+"F0.wireOp",EDGE,"E11.1.0");var subQ2=sQuery(id+"F0.wireOp",EDGE,"E2");var subQ3=sQuery(id+"F0.wireOp",EDGE,"E1");var subQ4=sQuery(id+"F0.wireOp",EDGE,"E0");Q0=makeQuery(id+"F13.boolean.opBoolean","MERGE",FACE,{"derivedFrom":[makeQuery(id+"F11.boolean.opBoolean","MERGE",FACE,{"derivedFrom":[makeQuery(id+"F7.boolean.opBoolean","MERGE",FACE,{"derivedFrom":[makeQuery(id+"F4.boolean.opBoolean","MERGE",FACE,{"derivedFrom":[makeQuery(id+"F1.opExtrude","CAP_FACE",FACE,{"disambiguationData":[OSD([subQ4,subQ3,subQ2,sQuery(id+"F0.wireOp",EDGE,"E3.0"),sQuery(id+"F0.wireOp",EDGE,"E4.0"),sQuery(id+"F0.wireOp",EDGE,"E5.0"),sQuery(id+"F0.wireOp",EDGE,"E7.filletArc"),sQuery(id+"F0.wireOp",EDGE,"E8.filletArc"),sQuery(id+"F0.wireOp",EDGE,"E9.filletArc"),sQuery(id+"F0.wireOp",EDGE,"E10.filletArc"),subQ1,sQuery(id+"F0.wireOp",EDGE,"E11.1.3"),sQuery(id+"F0.wireOp",EDGE,"E11.1.4"),sQuery(id+"F0.wireOp",EDGE,"E11.1.5"),sQuery(id+"F0.wireOp",EDGE,"E11.4.0"),sQuery(id+"F0.wireOp",EDGE,"E11.4.1"),sQuery(id+"F0.wireOp",EDGE,"E11.4.2"),subQ0])],"isStart":false}),makeQuery(id+"F4.opExtrude","CAP_FACE",FACE,{"disambiguationData":[OSD([subQ4,subQ3,subQ2,subQ1,sQuery(id+"F0.wireOp",EDGE,"E11.1.1"),sQuery(id+"F0.wireOp",EDGE,"E11.1.2"),sQuery(id+"F0.wireOp",EDGE,"E11.4.3"),sQuery(id+"F0.wireOp",EDGE,"E11.4.4"),sQuery(id+"F0.wireOp",EDGE,"E11.4.5"),subQ0])],"isStart":false})]}),makeQuery(id+"F7.opExtrude","CAP_FACE",FACE,{"disambiguationData":[OSD([sQuery(id+"F6.wireOp",EDGE,"E74"),sQuery(id+"F6.wireOp",EDGE,"E75"),sQuery(id+"F6.wireOp",EDGE,"E76"),sQuery(id+"F6.wireOp",EDGE,"E79"),sQuery(id+"F6.wireOp",EDGE,"E80"),sQuery(id+"F6.wireOp",EDGE,"E81"),sQuery(id+"F6.wireOp",EDGE,"E82"),sQuery(id+"F6.wireOp",EDGE,"E83"),sQuery(id+"F6.wireOp",EDGE,"E84"),sQuery(id+"F6.wireOp",EDGE,"E85"),sQuery(id+"F6.wireOp",EDGE,"E86"),sQuery(id+"F6.wireOp",EDGE,"E87"),sQuery(id+"F6.wireOp",EDGE,"E88"),sQuery(id+"F6.wireOp",EDGE,"E89"),sQuery(id+"F6.wireOp",EDGE,"E90")])],"isStart":true}),makeQuery(id+"F7.opExtrude","CAP_FACE",FACE,{"disambiguationData":[OSD([sQuery(id+"F6.wireOp",EDGE,"E93.MirrorCS"),sQuery(id+"F6.wireOp",EDGE,"E94.MirrorCS"),sQuery(id+"F6.wireOp",EDGE,"E95.MirrorCS"),sQuery(id+"F6.wireOp",EDGE,"E96.MirrorCS"),sQuery(id+"F6.wireOp",EDGE,"E97.MirrorCS"),sQuery(id+"F6.wireOp",EDGE,"E98.MirrorCS"),sQuery(id+"F6.wireOp",EDGE,"E99.MirrorCS"),sQuery(id+"F6.wireOp",EDGE,"E100.MirrorCS"),sQuery(id+"F6.wireOp",EDGE,"E101.MirrorCS"),sQuery(id+"F6.wireOp",EDGE,"E102.MirrorCS"),sQuery(id+"F6.wireOp",EDGE,"E103.MirrorCS"),sQuery(id+"F6.wireOp",EDGE,"E104.MirrorCS"),sQuery(id+"F6.wireOp",EDGE,"E105.MirrorCS"),sQuery(id+"F6.wireOp",EDGE,"E106.MirrorCS"),sQuery(id+"F6.wireOp",EDGE,"E107.MirrorCS")])],"isStart":true})]}),makeQuery(id+"F11.opExtrude","CAP_FACE",FACE,{"disambiguationData":[OSD([sQuery(id+"F10.wireOp",EDGE,"E113")])],"isStart":true}),makeQuery(id+"F11.opExtrude","CAP_FACE",FACE,{"disambiguationData":[OSD([sQuery(id+"F10.wireOp",EDGE,"E114.MirrorC")])],"isStart":true})]}),makeQuery(id+"F13.opExtrude","CAP_FACE",FACE,{"disambiguationData":[OSD([sQuery(id+"F12.wireOp",EDGE,"E115"),sQuery(id+"F12.wireOp",EDGE,"E116"),sQuery(id+"F12.wireOp",EDGE,"E117"),sQuery(id+"F12.wireOp",EDGE,"E118")])],"isStart":true}),makeQuery(id+"F13.opExtrude","CAP_FACE",FACE,{"disambiguationData":[OSD([sQuery(id+"F12.wireOp",EDGE,"E119.MirrorCS"),sQuery(id+"F12.wireOp",EDGE,"E120.MirrorCS"),sQuery(id+"F12.wireOp",EDGE,"E121.MirrorCS"),sQuery(id+"F12.wireOp",EDGE,"E122.MirrorCS")])],"isStart":true})]});}
            var sketch = newSketch(context, id + "F14", { "sketchPlane" : qUnion([Q0])});
            skCircle(sketch, "E123", {"center": v(0, 0) * mm, "radius": 10.97 * mm});
            skSolve(sketch);
        }
        {
            var Q0;
            Q0 = qSketchRegion(id + "F14", true);
            extrude(context, id + "F15", {"entities" : qUnion([Q0]), "operationType" : NewBodyOperationType.ADD, "oppositeDirection" : true, "depth" : 4 * mm, "offsetDistance" : 25 * mm});
        }
        {
            var Q0;
            Q0 = qSketchRegion(id + "F14", true);
            extrude(context, id + "F16", {"entities" : qUnion([Q0]), "operationType" : NewBodyOperationType.ADD, "depth" : 4 * mm, "offsetDistance" : 25 * mm});
        }
        {
            var Q0;
            Q0=makeQuery(id+"F16.opExtrude","CAP_FACE",FACE,{"disambiguationData":[OSD([sQuery(id+"F14.wireOp",EDGE,"E123")])],"isStart":false});
            var sketch = newSketch(context, id + "F17", { "sketchPlane" : qUnion([Q0])});
            skCircle(sketch, "E124", {"center": v(0, 0) * mm, "radius": 6 * mm});
            skCircle(sketch, "E125", {"center": v(0, 0) * mm, "radius": 7.97 * mm});
            skSolve(sketch);
        }
        {
            var Q0;
            Q0=makeQuery(id+"F17.imprint","IMPRINT",FACE,{"disambiguationData":[TD([[makeQuery(id+"F17.imprint","IMPRINT",EDGE,{"derivedFrom":sQuery(id+"F17.wireOp",EDGE,"E124")}),-1.0]])]});
            var Q1;
            Q1=makeQuery(id+"F17.imprint","IMPRINT",FACE,{"disambiguationData":[TD([[makeQuery(id+"F17.imprint","IMPRINT",EDGE,{"derivedFrom":sQuery(id+"F17.wireOp",EDGE,"E124")}),1.0]])]});
            extrude(context, id + "F18", {"entities" : qUnion([Q0, Q1]), "operationType" : NewBodyOperationType.REMOVE, "flatOperationType" : FlatOperationType.REMOVE, "thickness1" : 5 * mm, "thickness2" : 0 * mm, "thickness" : 5 * mm, "oppositeDirection" : true, "depth" : 5.75 * mm, "offsetDistance" : 25 * mm, "startOffsetBound" : StartOffsetType.BLIND, "startOffsetDistance" : 25 * mm, "domain" : OperationDomain.MODEL});
        }
        {
            var Q0;
            Q0=makeQuery(id+"F17.imprint","IMPRINT",FACE,{"disambiguationData":[TD([[makeQuery(id+"F17.imprint","IMPRINT",EDGE,{"derivedFrom":sQuery(id+"F17.wireOp",EDGE,"E124")}),1.0]])]});
            extrude(context, id + "F19", {"entities" : qUnion([Q0]), "operationType" : NewBodyOperationType.REMOVE, "oppositeDirection" : true, "depth" : 25 * mm, "offsetDistance" : 25 * mm});
        }
        {
            var Q0;
            Q0 = qSketchRegion(id + "F9", true);
            var Q1;
            Q1=sQuery(id+"F9.wireOp",EDGE,"E112");
            revolve(context, id + "F20", {"operationType" : NewBodyOperationType.REMOVE, "surfaceOperationType" : NewSurfaceOperationType.NEW, "entities" : qUnion([Q0]), "axis" : qUnion([Q1]), "revolveType" : RevolveType.FULL, "oppositeDirection" : true});
        }
    });
